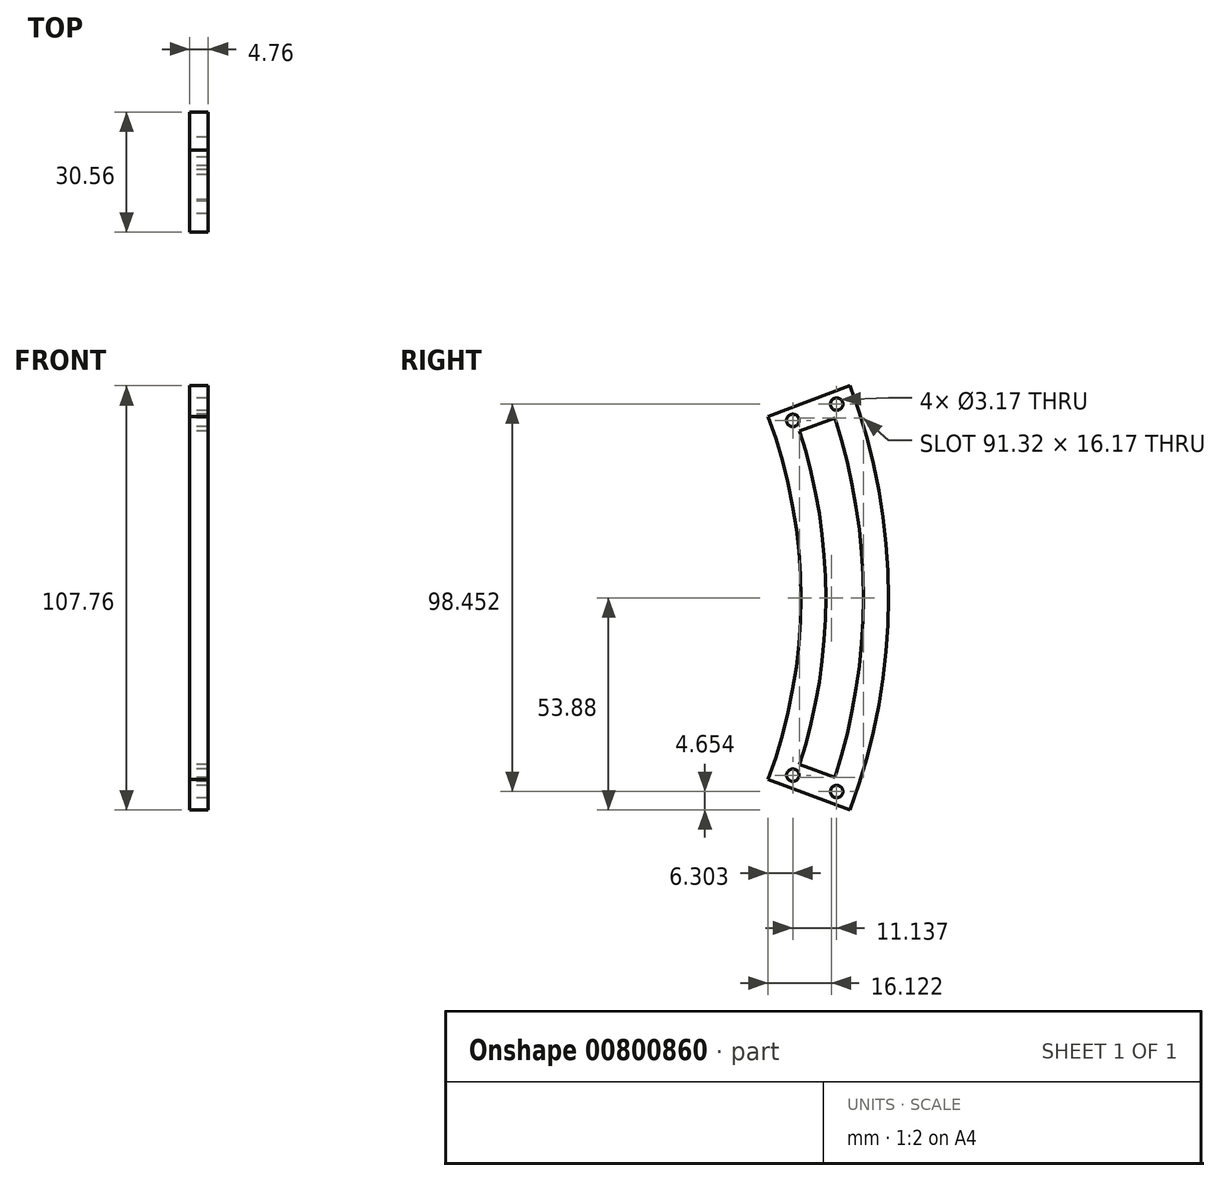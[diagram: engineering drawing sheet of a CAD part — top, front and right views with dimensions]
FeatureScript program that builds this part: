
annotation { "Feature Type Name" : "Feature", "Feature Type Description" : "" }
export const myFeature = defineFeature(function(context is Context, id is Id, definition is map)
    precondition{}
    {
        {
            var Q0;
            Q0=qCreatedBy(makeId("Right.planeOp"),FACE);
            var sketch = newSketch(context, id + "F0", { "sketchPlane" : qUnion([Q0])});
            skArc(sketch, "E0", {"start": v(133.84, 50) * mm, "mid": v(142.88, 0) * mm, "end": v(133.84, -50) * mm, "construction": true});
            skLineSegment(sketch, "E1", {"start": v(0, 0) * mm, "end": v(142.88, 0) * mm, "construction": true});
            skArc(sketch, "E2.0", {"start": v(131.47, 42.32) * mm, "mid": v(138.11, 0) * mm, "end": v(131.47, -42.32) * mm});
            skArc(sketch, "E3.0", {"start": v(140.4, 45.66) * mm, "mid": v(147.64, 0) * mm, "end": v(140.4, -45.66) * mm});
            skArc(sketch, "E4", {"start": v(123.43, 46.1) * mm, "mid": v(131.76, 0) * mm, "end": v(123.43, -46.1) * mm});
            skArc(sketch, "E5", {"start": v(144.25, -53.88) * mm, "mid": v(153.99, 0) * mm, "end": v(144.25, 53.88) * mm});
            skLineSegment(sketch, "E6", {"start": v(142.88, 0) * mm, "end": v(133.84, 50) * mm, "construction": true});
            skLineSegment(sketch, "E7", {"start": v(144.25, 53.88) * mm, "end": v(123.43, 46.1) * mm});
            skLineSegment(sketch, "E8.0", {"start": v(146.48, 47.93) * mm, "end": v(146.35, 47.88) * mm});
            skPoint(sketch, "E9.orphan", {"position": v(0, 131.76) * mm});
            skPoint(sketch, "E10.orphan", {"position": v(0, 142.88) * mm});
            skPoint(sketch, "E11.orphan", {"position": v(0, 153.99) * mm});
            skLineSegment(sketch, "E12.MirrorCS", {"start": v(144.25, -53.88) * mm, "end": v(123.43, -46.1) * mm});
            skLineSegment(sketch, "E13.MirrorCS", {"start": v(146.48, -47.93) * mm, "end": v(146.35, -47.88) * mm});
            skLineSegment(sketch, "E14.trimOffspring", {"start": v(140.4, 45.66) * mm, "end": v(131.47, 42.32) * mm});
            skPoint(sketch, "E15.orphan", {"position": v(0, -131.76) * mm});
            skPoint(sketch, "E16.orphan", {"position": v(0, -142.88) * mm});
            skPoint(sketch, "E17.orphan", {"position": v(0, -147.64) * mm});
            skPoint(sketch, "E18.orphan", {"position": v(0, -153.99) * mm});
            skPoint(sketch, "E19.trimOffspring.end.orphan", {"position": v(125.66, -40.15) * mm});
            skLineSegment(sketch, "E20.trimOffspring", {"start": v(140.4, -45.66) * mm, "end": v(131.47, -42.32) * mm});
            skPoint(sketch, "E21.orphan", {"position": v(125.66, 40.15) * mm});
            skLineSegment(sketch, "E22.0", {"start": v(145.36, 50.9) * mm, "end": v(124.54, 43.13) * mm, "construction": true});
            skLineSegment(sketch, "E23", {"start": v(134.92, 47) * mm, "end": v(124.54, 43.13) * mm});
            skCircle(sketch, "E24", {"center": v(129.73, 45.07) * mm, "radius": 1.59 * mm});
            skLineSegment(sketch, "E25", {"start": v(134.92, 47) * mm, "end": v(140.87, 49.23) * mm, "construction": true});
            skCircle(sketch, "E26", {"center": v(140.87, 49.23) * mm, "radius": 1.59 * mm});
            skCircle(sketch, "E27.MirrorC", {"center": v(129.73, -45.07) * mm, "radius": 1.59 * mm});
            skCircle(sketch, "E28.MirrorC", {"center": v(140.87, -49.23) * mm, "radius": 1.59 * mm});
            skSolve(sketch);
        }
        {
            var Q0;
            Q0=qSketchRegion(id+"F0",true);
            extrude(context, id + "F1", {"entities" : qUnion([Q0]), "depth" : 4.76 * mm, "offsetDistance" : 25 * mm});
        }
    });
